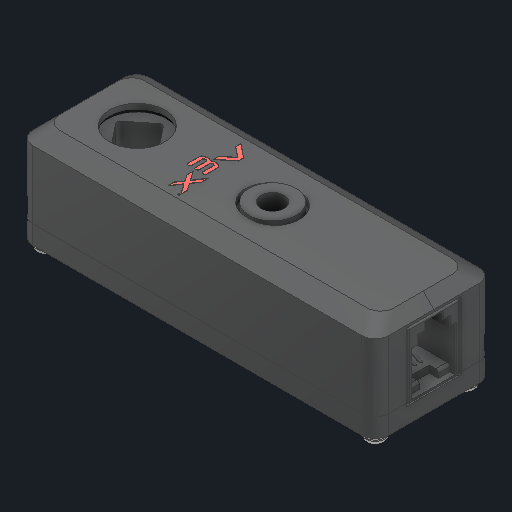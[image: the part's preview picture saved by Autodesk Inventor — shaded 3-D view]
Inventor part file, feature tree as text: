
AUTODESK INVENTOR PART (.ipt)
format: ipt  version: 2025 (Build 290162000, 162)  size: 3,137,024 bytes
history: native  units: in
note: dims shown in document units (in); Inventor stores cm internally (conversion verified against a paired STEP export)
features: other x12, sketch x1
ambient origin geometry x8: Origin, YZ Plane, XZ Plane, XY Plane, X Axis, Y Axis, Z Axis, Center Point
bodies: Solid1 (feature_tree), Solid2 (feature_tree), Solid3 (feature_tree), Solid4 (feature_tree), Solid5 (feature_tree), Solid6 (feature_tree), Solid7 (feature_tree), Solid8 (feature_tree), Solid9 (feature_tree), Solid10 (feature_tree)
feature tree (13):
  other  "V5 Rotation Sensor.ipt"
  other  "Solid1::V5 Rotation Sensor.ipt"
  other  "Solid2::V5 Rotation Sensor.ipt"
  other  "Solid3::V5 Rotation Sensor.ipt"
  other  "Solid4::V5 Rotation Sensor.ipt"
  other  "Solid5::V5 Rotation Sensor.ipt"
  other  "Solid6::V5 Rotation Sensor.ipt"
  other  "Solid7::V5 Rotation Sensor.ipt"
  other  "Solid8::V5 Rotation Sensor.ipt"
  other  "Solid9::V5 Rotation Sensor.ipt"
  other  "Solid10::V5 Rotation Sensor.ipt"
  other  "TaggingFeature1"
  sketch  "Sketch1"  dims[d0=0.3937in]
